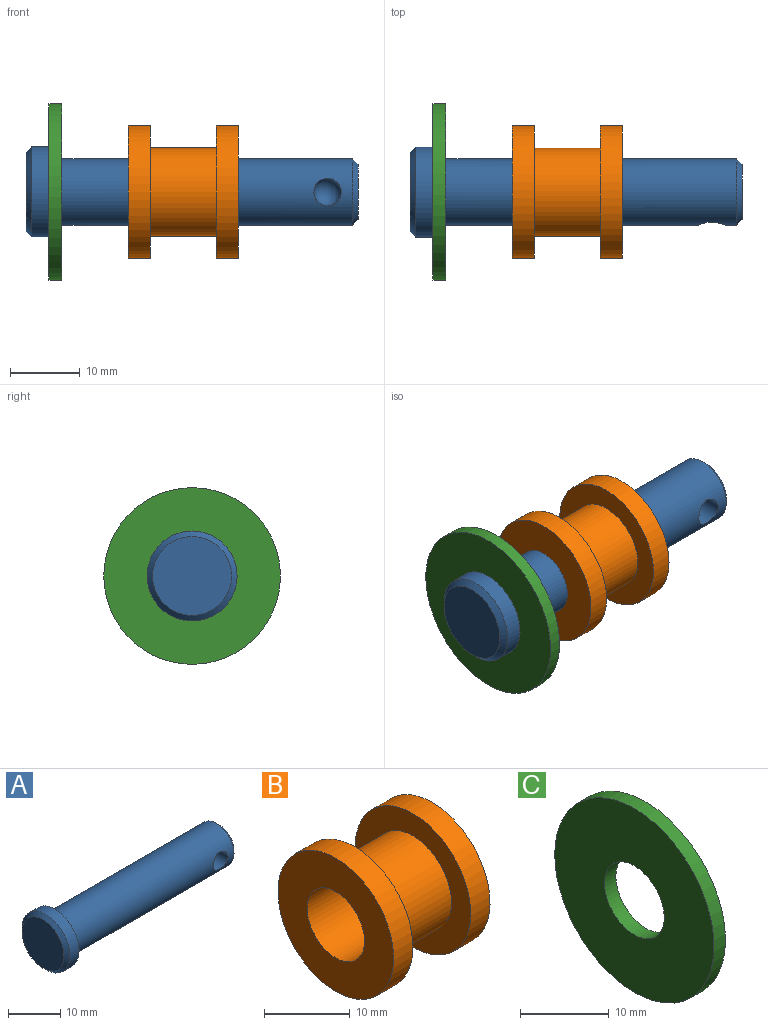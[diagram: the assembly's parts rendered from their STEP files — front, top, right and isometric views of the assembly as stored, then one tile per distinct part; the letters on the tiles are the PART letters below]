
ASSEMBLY  parts=3 mates=4
PART A: 9 faces, bbox 47.8x13x13 mm
  f0: cylinder r=4.76mm len=43.66mm, axis (-1,0,0), area 1293.7mm2, adj f2,f5,f8
  f1: plane 7.94x7.94mm, normal (1,0,0), area 49.5mm2, adj f8
  f2: plane 12.95x12.95mm, normal (1,0,0), area 60.5mm2, adj f0,f3
  f3: cylinder r=6.48mm len=12.95mm, axis (-1,0,0), area 102.1mm2, adj f2,f7
  f4: plane 11.37x11.37mm, normal (-1,0,0), area 101.5mm2, adj f7
  f5: cylinder r=1.98mm len=4.76mm, axis (0,1,0), area 56.7mm2, adj f0,f6
  f6: sphere r=1.98mm, area 24.7mm2, adj f5
  f7: cone r=5.68mm half-angle=45deg, axis (1,0,0), area 42.9mm2, adj f3,f4
  f8: cone r=4.76mm half-angle=45deg, axis (-1,0,0), area 30.8mm2, adj f0,f1
PART B: 8 faces, bbox 15.9x19.1x19.1 mm
  f0: cylinder r=6.35mm len=12.7mm, axis (-1,0,0), area 380mm2, adj f1,f7
  f1: plane 19.05x19.05mm, normal (1,0,0), area 158.3mm2, adj f0,f2
  f2: cylinder r=9.53mm len=19.05mm, axis (-1,0,0), area 190mm2, adj f1,f3
  f3: plane 19.05x19.05mm, normal (-1,0,0), area 214.5mm2, adj f2,f4
  f4: cylinder r=4.74mm len=15.88mm, axis (-1,0,0), area 472.5mm2, adj f3,f5
  f5: plane 19.05x19.05mm, normal (1,0,0), area 214.5mm2, adj f4,f6
  f6: cylinder r=9.53mm len=19.05mm, axis (-1,0,0), area 190mm2, adj f5,f7
  f7: plane 19.05x19.05mm, normal (-1,0,0), area 158.3mm2, adj f0,f6
PART C: 4 faces, bbox 1.8x25.4x25.4 mm
  f0: cylinder r=4.78mm len=9.55mm, axis (-1,0,0), area 54.9mm2, adj f2,f3
  f1: cylinder r=12.7mm len=25.4mm, axis (-1,0,0), area 145.9mm2, adj f2,f3
  f2: plane 25.4x25.4mm, normal (1,0,0), area 435.1mm2, adj f0,f1
  f3: plane 25.4x25.4mm, normal (-1,0,0), area 435.1mm2, adj f0,f1
PLACE A rot(axis=(0,0,1),0deg) t=(0,0,0)mm
PLACE B rot(axis=(0,-0.71,0.71),180deg) t=(27.38,0,0)mm
PLACE C t=(4.22,0,0)mm
MATE cylindrical B.f0 <-> A.f0  axis (-1,0,0) through (14.68,0,0)mm
MATE planar A.f0 <-> C.f0  axis (1,0,0) through (3.3,0,0)mm
MATE cylindrical C.f0 <-> A.f0  axis (-1,0,0) through (3.3,0,0)mm
MATE planar B.f0 <-> C.f0  axis (-1,0,0) through (14.68,0,0)mm
